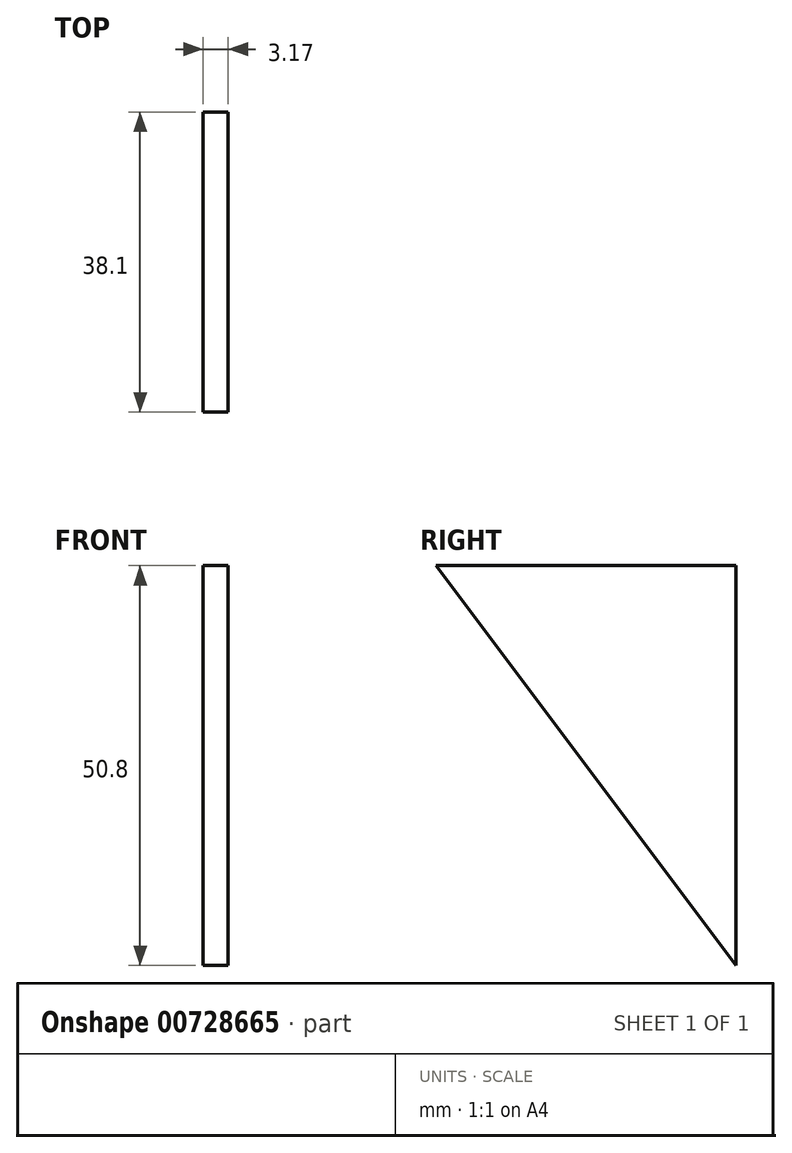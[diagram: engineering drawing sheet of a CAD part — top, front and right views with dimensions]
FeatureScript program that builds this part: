
annotation { "Feature Type Name" : "Feature", "Feature Type Description" : "" }
export const myFeature = defineFeature(function(context is Context, id is Id, definition is map)
    precondition{}
    {
        {
            var Q0;
            Q0=qCreatedBy(makeId("Right.planeOp"),FACE);
            var sketch = newSketch(context, id + "F0", { "sketchPlane" : qUnion([Q0])});
            skLineSegment(sketch, "E0", {"start": v(0, 0) * mm, "end": v(-38.1, 0) * mm});
            skLineSegment(sketch, "E1", {"start": v(-38.1, 0) * mm, "end": v(0, -50.8) * mm});
            skLineSegment(sketch, "E2", {"start": v(0, -50.8) * mm, "end": v(0, 0) * mm});
            skSolve(sketch);
        }
        {
            var Q0;
            Q0=makeQuery(id+"F0.imprint","IMPRINT",FACE,{"disambiguationData":[TD([[makeQuery(id+"F0.imprint","IMPRINT",EDGE,{"derivedFrom":sQuery(id+"F0.wireOp",EDGE,"E0")}),1.0]])]});
            extrude(context, id + "F1", {"entities" : qUnion([Q0]), "depth" : 3.17 * mm, "offsetDistance" : 25.4 * mm});
        }
    });
